# Revit family: 651_616ab1d17c3242239c3d3b346eebc3
name_source: partatom
category: Data Devices
revit_build: Autodesk Revit 2018 (Build: 20170223_1515(x64)
units: mm (PartAtom-declared; Revit-internal decimal feet)

## family parameters
Cut with Voids When Loaded = No
Host = Face
Maintain Annotation Orientation = Yes
Part Type = Normal
Room Calculation Point = No
Round Connector Dimension = Use Diameter
Shared = No

## types (1)
- 9416
    Default Elevation = 0 mm  [stored 0 ft]
    Description = Control panel CI600 white
    H1 = 40 mm  [stored 0.131234 ft]
    HT2 = 51 mm
    L2D = 0 mm  [stored 0 ft]
    LT2 = 42 mm
    LT3 = 21 mm
    MC Active Power = 0 W
    MC CosPhi = 0.95
    MC Number of Poles = 1
    MC Product Code = 9416
    MC Voltage = 230 V
    Manufacturer = Flexit
    R1 = 13 mm  [stored 0.0426509 ft]
    R2 = 15 mm  [stored 0.0492126 ft]
    SketchPlaneIDs = 10482;153b746f-b00a-47b6-946a-48530699bbd5-000028f2
    W1 = 11 mm
    W1__ve = -11 mm
    W2 = 6 mm  [stored 0.019685 ft]
    W2D = 0 mm  [stored 0 ft]
    W3 = 9 mm  [stored 0.0295276 ft]
    WT = 3 mm  [stored 0.00984252 ft]
    Z1 = 20 mm  [stored 0.0656168 ft]
    magiApparentLoad = 0 VA
    magiPartTypeId = 651
    magiProductFamilyId = 616ab1d17c3242239c3d3b346eebc3
    magiProductId = e72c7492156642c896aa1aa2b268eb

note: [stored X ft] marks values corroborated as IEEE doubles in the binary element streams (Revit-internal decimal feet)

## geometry (parser evidence)
native form markers: Sweep x2
no freeform markers — native parametric forms only
